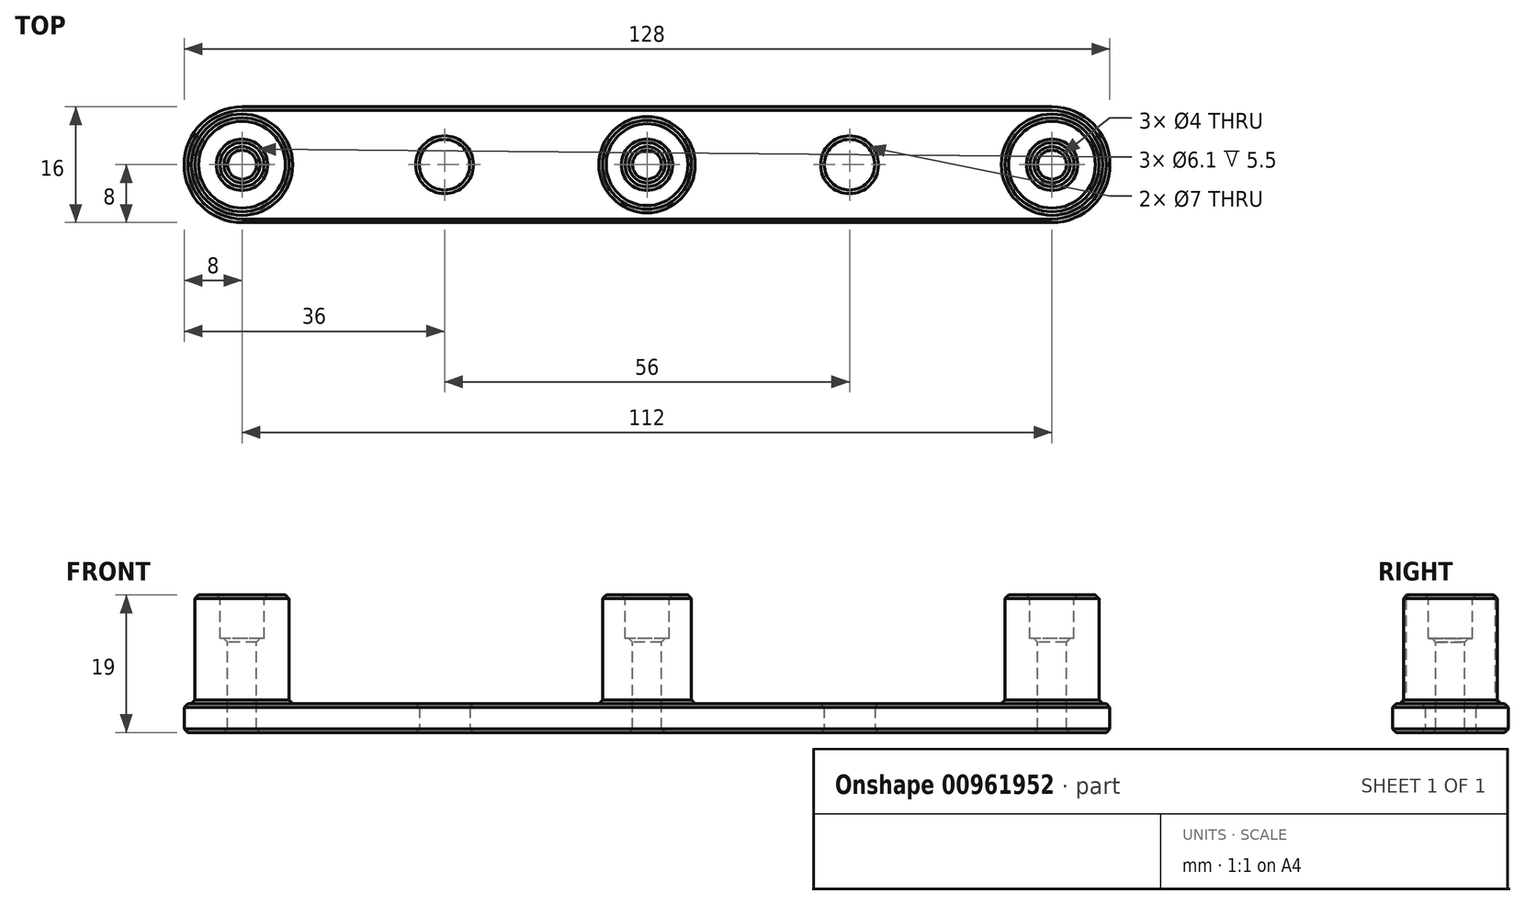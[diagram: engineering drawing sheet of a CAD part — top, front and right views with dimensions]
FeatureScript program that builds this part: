
annotation { "Feature Type Name" : "Feature", "Feature Type Description" : "" }
export const myFeature = defineFeature(function(context is Context, id is Id, definition is map)
    precondition{}
    {
        {
            var Q0;
            Q0=qCreatedBy(makeId("Top.planeOp"),FACE);
            var sketch = newSketch(context, id + "F0", { "sketchPlane" : qUnion([Q0])});
            skArc(sketch, "E0", {"start": v(56, -8) * mm, "mid": v(64, 0) * mm, "end": v(56, 8) * mm});
            skArc(sketch, "E1", {"start": v(-56, 8) * mm, "mid": v(-64, 0) * mm, "end": v(-56, -8) * mm});
            skLineSegment(sketch, "E2", {"start": v(-56, 0) * mm, "end": v(0, 0) * mm, "construction": true});
            skLineSegment(sketch, "E3", {"start": v(0, 0) * mm, "end": v(56, 0) * mm, "construction": true});
            skLineSegment(sketch, "E4", {"start": v(-56, 8) * mm, "end": v(56, 8) * mm});
            skLineSegment(sketch, "E5", {"start": v(-56, -8) * mm, "end": v(56, -8) * mm});
            skCircle(sketch, "E6", {"center": v(-28, 0) * mm, "radius": 3.5 * mm});
            skCircle(sketch, "E7", {"center": v(28, 0) * mm, "radius": 3.5 * mm});
            skSolve(sketch);
        }
        {
            var Q0;
            Q0 = qSketchRegion(id + "F0", true);
            extrude(context, id + "F1", {"entities" : qUnion([Q0]), "depth" : 4 * mm, "offsetDistance" : 25 * mm});
        }
        {
            var Q0;
            Q0=makeQuery(id+"F1.opExtrude","CAP_FACE",FACE,{"disambiguationData":[OSD([sQuery(id+"F0.wireOp",EDGE,"E0"),sQuery(id+"F0.wireOp",EDGE,"E1"),sQuery(id+"F0.wireOp",EDGE,"E4"),sQuery(id+"F0.wireOp",EDGE,"E5")])],"isStart":false});
            var sketch = newSketch(context, id + "F2", { "sketchPlane" : qUnion([Q0])});
            skCircle(sketch, "E8", {"center": v(-56, 0) * mm, "radius": 6.5 * mm});
            skCircle(sketch, "E9", {"center": v(56, 0) * mm, "radius": 6.5 * mm});
            skCircle(sketch, "E10", {"center": v(0, 0) * mm, "radius": 6.15 * mm});
            skSolve(sketch);
        }
        {
            var Q0;
            Q0 = qSketchRegion(id + "F2", true);
            extrude(context, id + "F3", {"entities" : qUnion([Q0]), "operationType" : NewBodyOperationType.ADD, "depth" : 15 * mm, "offsetDistance" : 25 * mm});
        }
        {
            var Q0;
            Q0=makeQuery(id+"F3.opExtrude","CAP_FACE",FACE,{"disambiguationData":[OSD([sQuery(id+"F2.wireOp",EDGE,"E10")])],"isStart":false});
            var sketch = newSketch(context, id + "F4", { "sketchPlane" : qUnion([Q0])});
            skCircle(sketch, "E11.0.0", {"center": v(56, 0) * mm, "radius": 6.5 * mm, "construction": true});
            skCircle(sketch, "E12.0.0", {"center": v(0, 0) * mm, "radius": 6.15 * mm, "construction": true});
            skCircle(sketch, "E13.0.0", {"center": v(-56, 0) * mm, "radius": 6.5 * mm, "construction": true});
            skCircle(sketch, "E14", {"center": v(56, 0) * mm, "radius": 2 * mm});
            skCircle(sketch, "E15", {"center": v(0, 0) * mm, "radius": 2 * mm});
            skCircle(sketch, "E16", {"center": v(-56, 0) * mm, "radius": 2 * mm});
            skSolve(sketch);
        }
        {
            var Q0;
            Q0 = qSketchRegion(id + "F4", true);
            extrude(context, id + "F5", {"entities" : qUnion([Q0]), "operationType" : NewBodyOperationType.REMOVE, "oppositeDirection" : true, "depth" : 25 * mm, "offsetDistance" : 25 * mm});
        }
        {
            var Q0;
            Q0=makeQuery(id+"F3.opExtrude","CAP_FACE",FACE,{"disambiguationData":[OSD([sQuery(id+"F2.wireOp",EDGE,"E8")])],"isStart":false});
            var sketch = newSketch(context, id + "F6", { "sketchPlane" : qUnion([Q0])});
            skCircle(sketch, "E17.0", {"center": v(-56, 0) * mm, "radius": 6.5 * mm, "construction": true});
            skCircle(sketch, "E18.0", {"center": v(0, 0) * mm, "radius": 6.15 * mm, "construction": true});
            skCircle(sketch, "E19.0", {"center": v(56, 0) * mm, "radius": 6.5 * mm, "construction": true});
            skCircle(sketch, "E20", {"center": v(-56, 0) * mm, "radius": 3.05 * mm});
            skCircle(sketch, "E21", {"center": v(0, 0) * mm, "radius": 3.05 * mm});
            skCircle(sketch, "E22", {"center": v(56, 0) * mm, "radius": 3.05 * mm});
            skSolve(sketch);
        }
        {
            var Q0;
            Q0 = qSketchRegion(id + "F6", true);
            extrude(context, id + "F7", {"entities" : qUnion([Q0]), "operationType" : NewBodyOperationType.REMOVE, "oppositeDirection" : true, "depth" : 6 * mm, "offsetDistance" : 25 * mm});
        }
        {
            var Q0;
            Q0=makeQuery(id+"F3.opExtrude","CAP_FACE",FACE,{"disambiguationData":[OSD([sQuery(id+"F2.wireOp",EDGE,"E8")])],"isStart":false});
            var Q1;
            Q1=makeQuery(id+"F3.opExtrude","CAP_FACE",FACE,{"disambiguationData":[OSD([sQuery(id+"F2.wireOp",EDGE,"E10")])],"isStart":false});
            var Q2;
            Q2=makeQuery(id+"F3.opExtrude","CAP_FACE",FACE,{"disambiguationData":[OSD([sQuery(id+"F2.wireOp",EDGE,"E9")])],"isStart":false});
            var Q3;
            Q3=makeQuery(id+"F1.opExtrude","CAP_FACE",FACE,{"disambiguationData":[OSD([sQuery(id+"F0.wireOp",EDGE,"E0"),sQuery(id+"F0.wireOp",EDGE,"E1"),sQuery(id+"F0.wireOp",EDGE,"E4"),sQuery(id+"F0.wireOp",EDGE,"E5")])],"isStart":false});
            var Q4;
            Q4=makeQuery(id+"F1.opExtrude","CAP_FACE",FACE,{"disambiguationData":[OSD([sQuery(id+"F0.wireOp",EDGE,"E0"),sQuery(id+"F0.wireOp",EDGE,"E1"),sQuery(id+"F0.wireOp",EDGE,"E4"),sQuery(id+"F0.wireOp",EDGE,"E5")])],"isStart":true});
            var Q5;
            Q5=makeQuery(id+"F7.boolean.opBoolean","INTERSECT",EDGE,{"derivedFrom":[makeQuery(id+"F5.boolean.opBoolean","COPY",FACE,{"derivedFrom":makeQuery(id+"F5.opExtrude","SWEPT_FACE",FACE,{"disambiguationData":[OSD([sQuery(id+"F4.wireOp",EDGE,"E16")])]})}),makeQuery(id+"F7.opExtrude","CAP_FACE",FACE,{"disambiguationData":[OSD([sQuery(id+"F6.wireOp",EDGE,"E20")])],"isStart":false})]});
            var Q6;
            Q6=makeQuery(id+"F7.boolean.opBoolean","INTERSECT",EDGE,{"derivedFrom":[makeQuery(id+"F5.boolean.opBoolean","COPY",FACE,{"derivedFrom":makeQuery(id+"F5.opExtrude","SWEPT_FACE",FACE,{"disambiguationData":[OSD([sQuery(id+"F4.wireOp",EDGE,"E15")])]})}),makeQuery(id+"F7.opExtrude","CAP_FACE",FACE,{"disambiguationData":[OSD([sQuery(id+"F6.wireOp",EDGE,"E21")])],"isStart":false})]});
            var Q7;
            Q7=makeQuery(id+"F7.boolean.opBoolean","INTERSECT",EDGE,{"derivedFrom":[makeQuery(id+"F5.boolean.opBoolean","COPY",FACE,{"derivedFrom":makeQuery(id+"F5.opExtrude","SWEPT_FACE",FACE,{"disambiguationData":[OSD([sQuery(id+"F4.wireOp",EDGE,"E14")])]})}),makeQuery(id+"F7.opExtrude","CAP_FACE",FACE,{"disambiguationData":[OSD([sQuery(id+"F6.wireOp",EDGE,"E22")])],"isStart":false})]});
            chamfer(context, id + "F8", {"entities" : qUnion([Q0, Q1, Q2, Q3, Q4, Q5, Q6, Q7]), "width" : .5 * mm, "tangentPropagation" : true});
        }
    });
